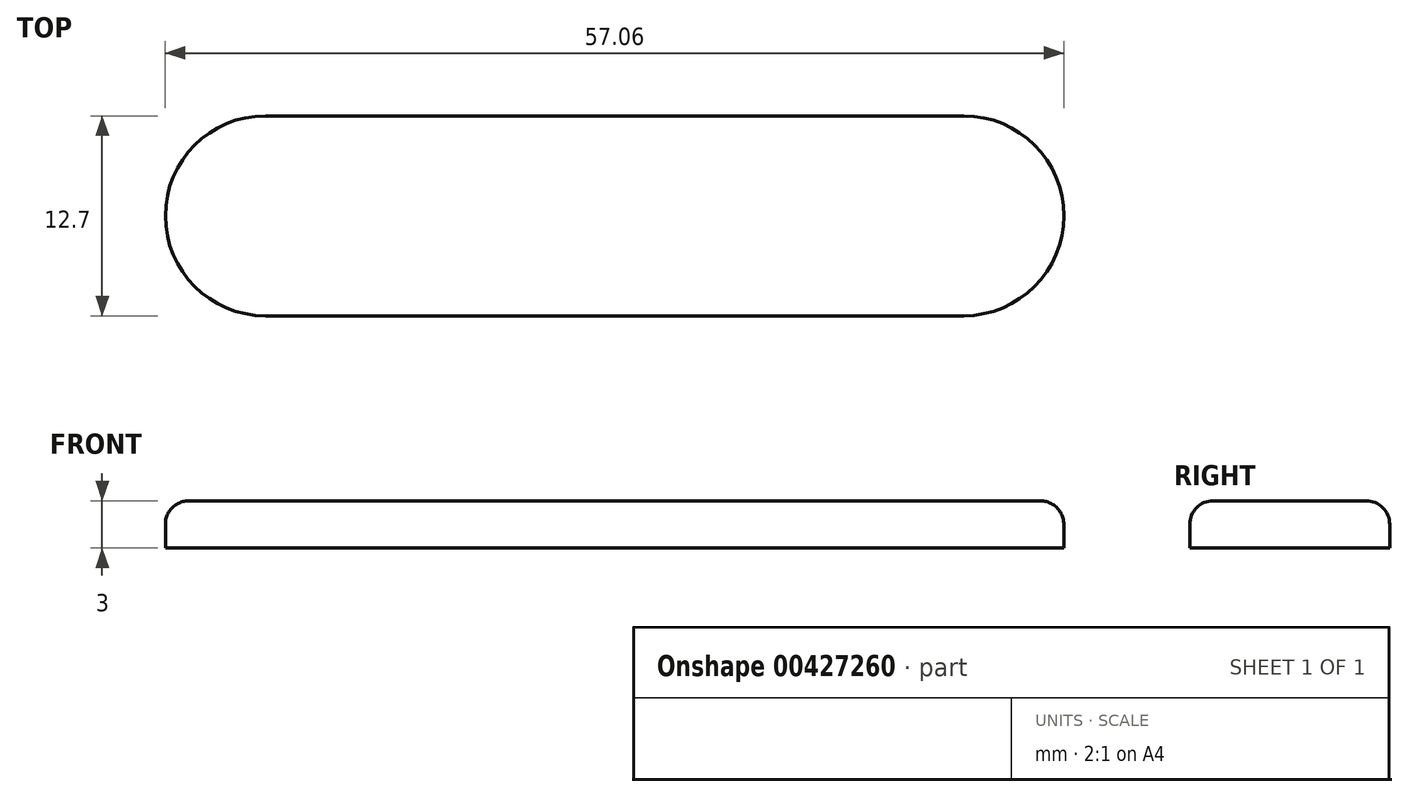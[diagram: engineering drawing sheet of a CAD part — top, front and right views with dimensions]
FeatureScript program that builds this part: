
annotation { "Feature Type Name" : "Feature", "Feature Type Description" : "" }
export const myFeature = defineFeature(function(context is Context, id is Id, definition is map)
    precondition{}
    {
        {
            var Q0;
            Q0=qCreatedBy(makeId("Top.planeOp"),FACE);
            var sketch = newSketch(context, id + "F0", { "sketchPlane" : qUnion([Q0])});
            skLineSegment(sketch, "E0.bottom", {"start": v(-12.04, -5.57) * mm, "end": v(32.32, -5.57) * mm});
            skLineSegment(sketch, "E0.top", {"start": v(-12.04, 7.13) * mm, "end": v(32.32, 7.13) * mm});
            skLineSegment(sketch, "E0.left", {"start": v(-12.04, -5.57) * mm, "end": v(-12.04, 7.13) * mm});
            skLineSegment(sketch, "E0.right", {"start": v(32.32, -5.57) * mm, "end": v(32.32, 7.13) * mm});
            skArc(sketch, "E1", {"start": v(32.32, -5.57) * mm, "mid": v(38.67, 0.78) * mm, "end": v(32.32, 7.13) * mm});
            skArc(sketch, "E2", {"start": v(-12.04, 7.13) * mm, "mid": v(-18.39, 0.78) * mm, "end": v(-12.04, -5.57) * mm});
            skSolve(sketch);
        }
        {
            var Q0;
            Q0 = qSketchRegion(id + "F0", true);
            extrude(context, id + "F1", {"entities" : qUnion([Q0]), "endBound" : BoundingType.SYMMETRIC, "depth" : 3 * mm});
        }
        {
            var Q0;
            Q0=makeQuery(id+"F1.opExtrude","CAP_EDGE",EDGE,{"disambiguationData":[OSD([sQuery(id+"F0.wireOp",EDGE,"Z9EMnrH0-Vb7P-z6Jp-Mg5i-nHgf34xhvm4A")])],"isStart":false});
            var Q1;
            Q1=makeQuery(id+"F1.opExtrude","CAP_EDGE",EDGE,{"disambiguationData":[OSD([sQuery(id+"F0.wireOp",EDGE,"E0.bottom")])],"isStart":false});
            var Q2;
            Q2=makeQuery(id+"F1.opExtrude","CAP_EDGE",EDGE,{"disambiguationData":[OSD([sQuery(id+"F0.wireOp",EDGE,"E0.top")])],"isStart":false});
            var Q3;
            Q3=makeQuery(id+"F1.opExtrude","CAP_EDGE",EDGE,{"disambiguationData":[OSD([sQuery(id+"F0.wireOp",EDGE,"E1")])],"isStart":false});
            fillet(context, id + "F2", {"entities" : qUnion([Q0, Q1, Q2, Q3]), "radius" : 1.5 * mm, "tangentPropagation" : true, "allowEdgeOverflow" : false});
        }
    });
